# Revit family: Power-ModularDevices-GEWISS-90MCB-MTC45_1PN
name_source: partatom
category: Apparecchi elettrici
revit_build: Autodesk Revit MEP 2016 (Build: 20150220_1215(x64)
units: mm (PartAtom-declared; Revit-internal decimal feet)

## family parameters
Condiviso = Sì
Host = Superficie
Mantenere orientamento annotazione = Sì
Numero OmniClass = 23.80.30.14
Punto di calcolo locali = Sì
Quota connettore circolare = Usa diametro
Taglio con vuoti quando caricato = No
Tipo di parte = Normale
Titolo OmniClass = Power Distribution

## types (8) — shared parameters
Altezza = 85 mm  [stored 0.278871 ft]
Breaking capacity (EN 60898) = 1 x Icn
Breaking capacity EN 60898 (Ics) = 1 x Icn
Breaking capacity EN 60898 230V (Icn) = 4500A
Breaking capacity EN 60947-2 (Ics) = 100% Icu
Breaking capacity EN 60947-2 230V (Icu) = 6KA
Carico apparente = 0 VA
Catalogue = POWER
Catalogue Range = 90 MCB
Curve = C
Description = COMPACT MINIATURE CIRCUIT BREAKER
Electrical endurance = 10000
Electrocod = 1411
Finitura = Grigio chiaro
IDF = 7a3b7c7f-80df-42a1-8709-a049bc15c2e7
IDT = 2dbc19b2-da5e-4e9f-9248-a6ecd1d38506
Immagine tipo = GW90031.jpg
Insulation voltage = 500V
Interuttore = Grigio scuro
Label = MTC 45
Larghezza = 18 mm  [stored 0.0590551 ft]
Maximum operating voltage = 440V AC / 220V DC
Mechanical endurance = 20.000
Minimum operating voltage = 12V ac/dc
No. modules = 1
No. of modules EN 50022 = 1
No. of poles = 1P+N
Number of poles = 1P+N
Numero di poli_ = 1
Operating temperature = -25 +60 °C
Parti incassate = Sì
Produttore = GEWISS S.p.A.
Prospetto di default = 1219 mm
Rated frequency (Hz) = 50/60 Hz
Rated impulse withstand voltage = 4KV
Rated insulation voltage (Ui) = 500V
Rated tightening torque = 1.2 Nm
Rated voltage = 230V
SEO = MCB
Section flexible cable = <=1x10 - <=2x6 mm²
Section rigid cable = <=1x16 - <=1x10+1x6 mm²
Spessore = 150 mm
Standard = EN 60898, EN 60947-2
Standard; = EN 60898, EN 60947-2
Stocking temperature = -40 +70 °C
Technical sheet = https://www.gewiss.com
URL = https://www.gewiss.com
Version file RFA = 19.0
Voltaggio = 230 V

## per-type parameters (varying)
| type | Descrizione | EAN code | Modello | Rated current (In) | Rated current: |
| GW90028 - COMPACT MCB 1P+N C20 4,5KA 1M | COMPACT MCB 1P+N C20 4,5KA 1M | 8011564056473 | GW90028 | 20A | 20A |
| GW90029 - COMPACT MCB 1P+N C25 4,5KA 1M | COMPACT MCB 1P+N C25 4,5KA 1M | 8011564056480 | GW90029 | 25A | 25A |
| GW90025 - COMPACT MCB 1P+N C6 4,5KA 1M | COMPACT MCB 1P+N C6 4,5KA 1M | 8011564056442 | GW90025 | 6A | 6A |
| GW90026 - COMPACT MCB 1P+N C10 4,5KA 1M | COMPACT MCB 1P+N C10 4,5KA 1M | 8011564056459 | GW90026 | 10A | 10A |
| GW90030 - COMPACT MCB 1P+N C32 4,5KA 1M | COMPACT MCB 1P+N C32 4,5KA 1M | 8011564056497 | GW90030 | 32A | 32A |
| GW90027 - COMPACT MCB 1P+N C16 4,5KA 1M | COMPACT MCB 1P+N C16 4,5KA 1M | 8011564056466 | GW90027 | 16A | 16A |
| GW90022 - COMPACT MCB 1P+N C2 4,5KA 1M | COMPACT MCB 1P+N C2 4,5KA 1M | 8011564228122 | GW90022 | 2A | 2A |
| GW90031 - COMPACT MCB 1P+N C13 4,5KA 1M | COMPACT MCB 1P+N C13 4,5KA 1M | 8011564225220 | GW90031 | 13A | 13A |

note: [stored X ft] marks values corroborated as IEEE doubles in the binary element streams (Revit-internal decimal feet)

## geometry (parser evidence)
native form markers: Sweep x2
no freeform markers — native parametric forms only
